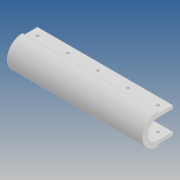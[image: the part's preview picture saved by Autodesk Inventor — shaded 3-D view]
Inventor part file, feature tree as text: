
AUTODESK INVENTOR PART (.ipt)
format: ipt  version: 2020 (Build 240168000, 168)  size: 128,512 bytes
history: native  units: mm
features: extrude x3, sketch x3, other x1, pattern_linear x1, mirror x1
ambient origin geometry x8: Origin, YZ Plane, XZ Plane, XY Plane, X Axis, Y Axis, Z Axis, Center Point
bodies: Body1 (feature_tree)
feature tree (9):
  other  "Твердое тело1"
  extrude  "Выдавливание1"  Depth=180.0mm
  extrude  "Выдавливание2"  Depth=20.0mm
  extrude  "Выдавливание3"  Depth=4.0mm TaperAngle=0.0deg
  pattern_linear  "Прямоуг.массив1"  Spacing1=3.0mm  [1 undecoded]
  mirror  "Зеркальное отражение1"
  sketch  "Эскиз1"
  sketch  "Эскиз2"
  sketch  "Эскиз3"
note: 1 required parameter value undecoded (feature->parameter linkage not recoverable at this tier; creation-order binding heuristic only, values carry confidence <= 0.55)
